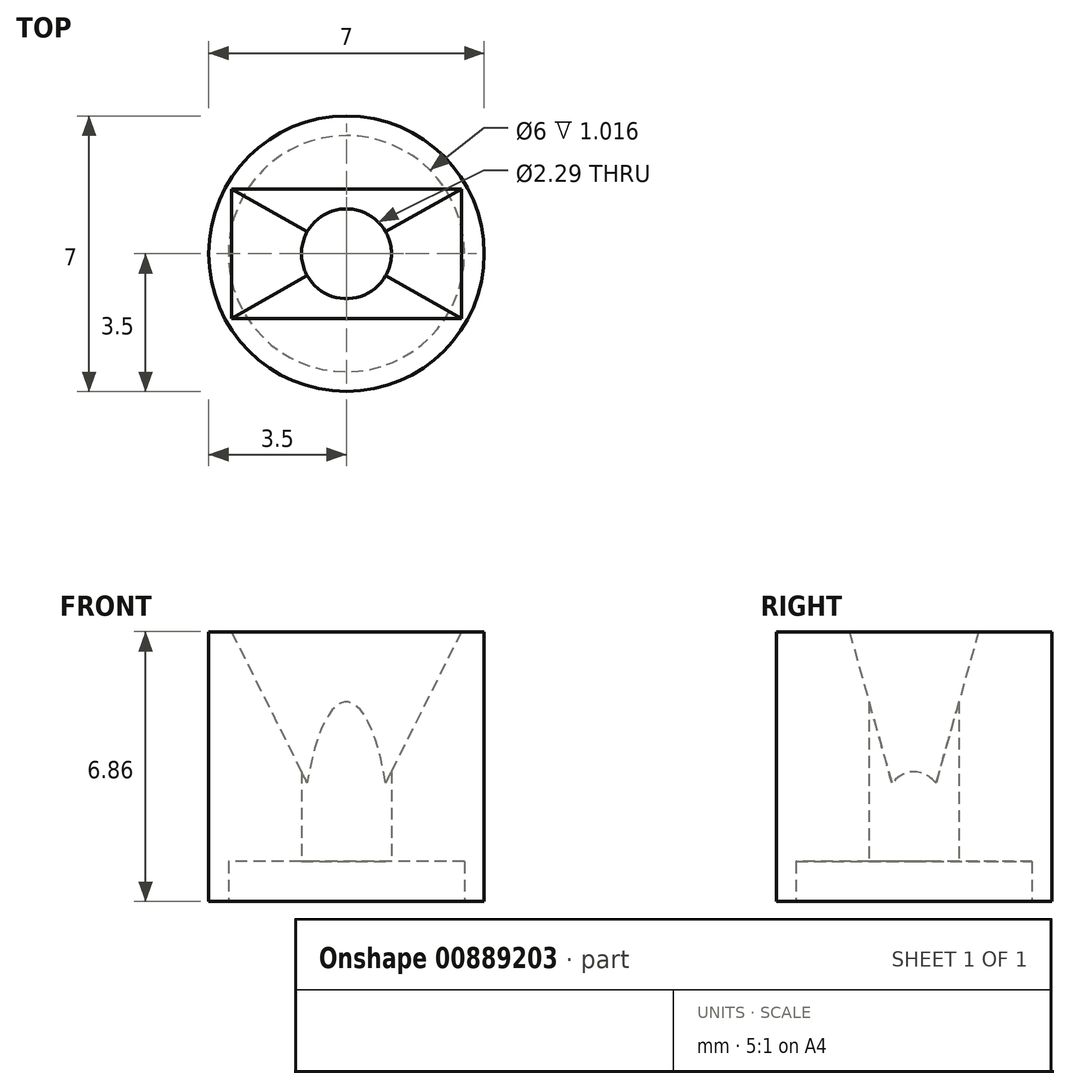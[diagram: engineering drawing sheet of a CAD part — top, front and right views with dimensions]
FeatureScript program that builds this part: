
annotation { "Feature Type Name" : "Feature", "Feature Type Description" : "" }
export const myFeature = defineFeature(function(context is Context, id is Id, definition is map)
    precondition{}
    {
        {
            var Q0;
            Q0=qCreatedBy(makeId("Top.planeOp"),FACE);
            var sketch = newSketch(context, id + "F0", { "sketchPlane" : qUnion([Q0])});
            skCircle(sketch, "E0", {"center": v(0, 0) * mm, "radius": 3 * mm});
            skCircle(sketch, "E1", {"center": v(0, 0) * mm, "radius": 3.5 * mm});
            skSolve(sketch);
        }
        {
            var Q0;
            Q0=qSketchRegion(id+"F0",true);
            extrude(context, id + "F1", {"entities" : qUnion([Q0]), "depth" : 17.02 * mm, "offsetDistance" : 25.4 * mm});
        }
        {
            var Q0;
            Q0=qCreatedBy(makeId("Top.planeOp"),FACE);
            cPlane(context, id + "F2", {"entities" : qUnion([Q0]), "cplaneType" : CPlaneType.OFFSET, "offset" : 1.02 * mm, "width" : 152.4 * mm, "height" : 152.4 * mm});
        }
        {
            var Q0;
            Q0=qCreatedBy(id+"F2.planeOp",FACE);
            var sketch = newSketch(context, id + "F3", { "sketchPlane" : qUnion([Q0])});
            skPoint(sketch, "E2", {"position": v(0, 0) * mm});
            skCircle(sketch, "E3", {"center": v(0, 0) * mm, "radius": 1.14 * mm});
            skCircle(sketch, "E4", {"center": v(0, 0) * mm, "radius": 3.5 * mm});
            skSolve(sketch);
        }
        {
            var Q0;
            Q0 = qSketchRegion(id + "F3", true);
            var Q1;
            Q1=makeQuery(id+"F1.opExtrude","CAP_FACE",FACE,{"disambiguationData":[OSD([sQuery(id+"F0.wireOp",EDGE,"E0"),sQuery(id+"F0.wireOp",EDGE,"E1")])],"isStart":false});
            extrude(context, id + "F4", {"entities" : qUnion([Q0]), "operationType" : NewBodyOperationType.ADD, "endBound" : BoundingType.UP_TO_SURFACE, "depth" : 25.4 * mm, "endBoundEntityFace" : qUnion([Q1]), "offsetDistance" : 25.4 * mm});
        }
        {
            var Q0;
            Q0=qCreatedBy(id+"F2.planeOp",FACE);
            cPlane(context, id + "F5", {"entities" : qUnion([Q0]), "cplaneType" : CPlaneType.OFFSET, "offset" : 16 * mm, "width" : 152.4 * mm, "height" : 152.4 * mm});
        }
        {
            var Q0;
            Q0=qCreatedBy(id+"F5.planeOp",FACE);
            var sketch = newSketch(context, id + "F6", { "sketchPlane" : qUnion([Q0])});
            skLineSegment(sketch, "E5.bottom", {"start": v(8, 4.5) * mm, "end": v(-8, 4.5) * mm});
            skLineSegment(sketch, "E5.top", {"start": v(8, -4.5) * mm, "end": v(-8, -4.5) * mm});
            skLineSegment(sketch, "E5.left", {"start": v(8, 4.5) * mm, "end": v(8, -4.5) * mm});
            skLineSegment(sketch, "E5.right", {"start": v(-8, 4.5) * mm, "end": v(-8, -4.5) * mm});
            skPoint(sketch, "E5.middle", {"position": v(0, 0) * mm});
            skSolve(sketch);
        }
        {
            var Q1;
            Q1=makeQuery(id+"F6.imprint","IMPRINT",FACE,{"disambiguationData":[TD([[makeQuery(id+"F6.imprint","IMPRINT",EDGE,{"derivedFrom":sQuery(id+"F6.wireOp",EDGE,"E5.bottom")}),1.0]])]});
            var Q2;
            Q2=sQuery(id+"F3.wireOp",VERTEX,"E2");
            loft(context, id + "F7", {"operationType" : NewBodyOperationType.REMOVE, "sheetProfilesArray" : [{ "sheetProfileEntities" : qUnion([Q1]) }, { "sheetProfileEntities" : qUnion([Q2]) }]});
        }
        {
            var Q0;
            Q0=qCreatedBy(id+"F5.planeOp",FACE);
            var sketch = newSketch(context, id + "F8", { "sketchPlane" : qUnion([Q0])});
            skCircle(sketch, "E6", {"center": v(0, 0) * mm, "radius": 4.12 * mm});
            skSolve(sketch);
        }
        {
            var Q0;
            Q0 = qSketchRegion(id + "F8", true);
            extrude(context, id + "F9", {"entities" : qUnion([Q0]), "operationType" : NewBodyOperationType.REMOVE, "oppositeDirection" : true, "depth" : 10.16 * mm, "offsetDistance" : 25.4 * mm});
        }
    });
